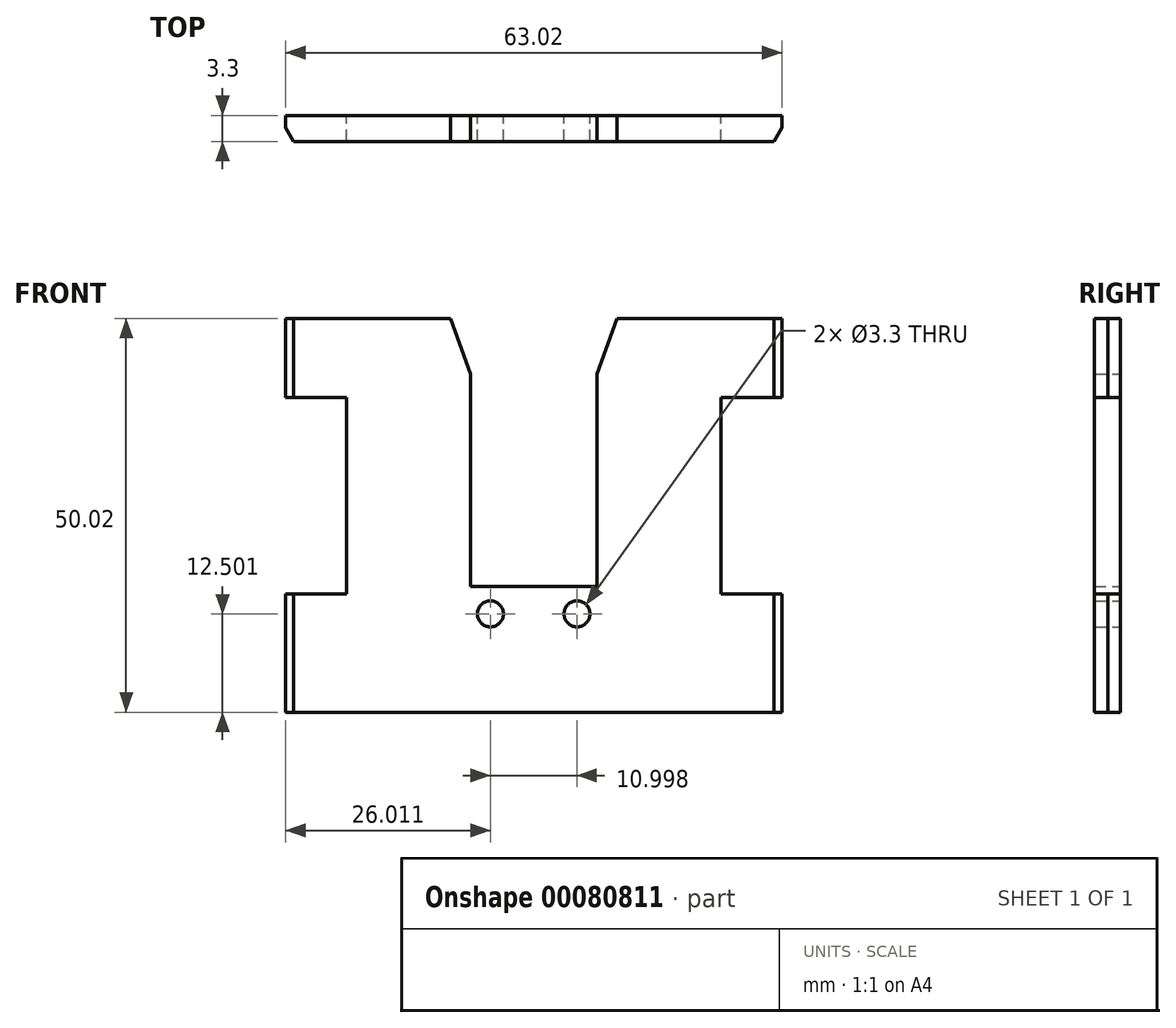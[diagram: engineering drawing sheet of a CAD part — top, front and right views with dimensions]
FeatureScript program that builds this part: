
annotation { "Feature Type Name" : "Feature", "Feature Type Description" : "" }
export const myFeature = defineFeature(function(context is Context, id is Id, definition is map)
    precondition{}
    {
        {
            var Q0;
            Q0=qCreatedBy(makeId("Front.planeOp"),FACE);
            var sketch = newSketch(context, id + "F0", { "sketchPlane" : qUnion([Q0])});
            skLineSegment(sketch, "E0.bottom", {"start": v(31.5, -7.5) * mm, "end": v(-31.5, -7.5) * mm});
            skLineSegment(sketch, "E0.top", {"start": v(31.5, 7.5) * mm, "end": v(23.76, 7.5) * mm});
            skLineSegment(sketch, "E0.left", {"start": v(31.5, -7.5) * mm, "end": v(31.5, 7.5) * mm});
            skLineSegment(sketch, "E0.right", {"start": v(-31.5, -7.5) * mm, "end": v(-31.5, 7.5) * mm});
            skPoint(sketch, "E0.middle", {"position": v(0, 0) * mm});
            skLineSegment(sketch, "E1.top", {"start": v(-23.76, 42.5) * mm, "end": v(-10.55, 42.5) * mm});
            skLineSegment(sketch, "E1.left", {"start": v(-23.76, 7.5) * mm, "end": v(-23.76, 32.5) * mm});
            skLineSegment(sketch, "E1.right", {"start": v(-8.01, 8.5) * mm, "end": v(-8.01, 35.5) * mm});
            skLineSegment(sketch, "E2.bottom", {"start": v(-23.76, 42.5) * mm, "end": v(-31.5, 42.5) * mm});
            skLineSegment(sketch, "E2.top", {"start": v(-23.76, 32.5) * mm, "end": v(-31.5, 32.5) * mm});
            skLineSegment(sketch, "E2.right", {"start": v(-31.5, 42.5) * mm, "end": v(-31.5, 32.5) * mm});
            skLineSegment(sketch, "E3.trimOffspring", {"start": v(-23.76, 7.5) * mm, "end": v(-31.5, 7.5) * mm});
            skLineSegment(sketch, "E4", {"start": v(0, 0) * mm, "end": v(0, 45.03) * mm});
            skLineSegment(sketch, "E5.MirrorCS", {"start": v(23.76, 7.5) * mm, "end": v(31.5, 7.5) * mm});
            skLineSegment(sketch, "E6.top", {"start": v(-8.01, 8.5) * mm, "end": v(8.01, 8.5) * mm});
            skCircle(sketch, "E7", {"center": v(-5.5, 5) * mm, "radius": 1.65 * mm});
            skCircle(sketch, "E8.MirrorC", {"center": v(5.5, 5) * mm, "radius": 1.65 * mm});
            skPoint(sketch, "E9", {"position": v(-8.01, 35.5) * mm});
            skPoint(sketch, "E10", {"position": v(-10.55, 42.5) * mm});
            skLineSegment(sketch, "E11", {"start": v(-10.55, 42.5) * mm, "end": v(-8.01, 35.5) * mm});
            skPoint(sketch, "E12.orphan", {"position": v(-8.01, 42.5) * mm});
            skLineSegment(sketch, "E13.MirrorCS", {"start": v(10.55, 42.5) * mm, "end": v(8.01, 35.5) * mm});
            skPoint(sketch, "E14.MirrorP", {"position": v(8.01, 42.5) * mm});
            skPoint(sketch, "E15.MirrorP", {"position": v(10.55, 42.5) * mm});
            skPoint(sketch, "E16.MirrorP", {"position": v(8.01, 35.5) * mm});
            skLineSegment(sketch, "E17.MirrorCS", {"start": v(31.5, 42.5) * mm, "end": v(31.5, 32.5) * mm});
            skLineSegment(sketch, "E18.MirrorCS", {"start": v(23.76, 42.5) * mm, "end": v(10.55, 42.5) * mm});
            skLineSegment(sketch, "E19.MirrorCS", {"start": v(23.76, 7.5) * mm, "end": v(23.76, 32.5) * mm});
            skLineSegment(sketch, "E20.MirrorCS", {"start": v(8.01, 8.5) * mm, "end": v(8.01, 35.5) * mm});
            skLineSegment(sketch, "E21.MirrorCS", {"start": v(23.76, 42.5) * mm, "end": v(31.5, 42.5) * mm});
            skLineSegment(sketch, "E22.MirrorCS", {"start": v(23.76, 32.5) * mm, "end": v(31.5, 32.5) * mm});
            skSolve(sketch);
        }
        {
            var Q0;
            Q0=makeQuery(id+"F0.imprint","IMPRINT",FACE,{"disambiguationData":[TD([[makeQuery(id+"F0.imprint","IMPRINT",EDGE,{"derivedFrom":sQuery(id+"F0.wireOp",EDGE,"E0.bottom")}),-1.0]])]});
            extrude(context, id + "F1", {"entities" : qUnion([Q0]), "endBound" : BoundingType.SYMMETRIC, "depth" : 3.3 * mm});
        }
        {
            var Q0;
            Q0=makeQuery(id+"F1.opExtrude","CAP_EDGE",EDGE,{"disambiguationData":[OSD([sQuery(id+"F0.wireOp",EDGE,"E0.left")])],"isStart":false});
            var Q1;
            Q1=makeQuery(id+"F1.opExtrude","CAP_EDGE",EDGE,{"disambiguationData":[OSD([sQuery(id+"F0.wireOp",EDGE,"E17.MirrorCS")])],"isStart":false});
            var Q2;
            Q2=makeQuery(id+"F1.opExtrude","CAP_EDGE",EDGE,{"disambiguationData":[OSD([sQuery(id+"F0.wireOp",EDGE,"E0.right")])],"isStart":false});
            var Q3;
            Q3=makeQuery(id+"F1.opExtrude","CAP_EDGE",EDGE,{"disambiguationData":[OSD([sQuery(id+"F0.wireOp",EDGE,"E2.right")])],"isStart":false});
            chamfer(context, id + "F2", {"entities" : qUnion([Q0, Q1, Q2, Q3]), "chamferType" : ChamferType.OFFSET_ANGLE, "width" : 1.02 * mm, "oppositeDirection" : false, "angle" : 60 * degree, "tangentPropagation" : true});
        }
    });
